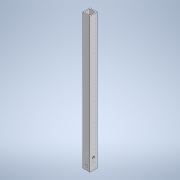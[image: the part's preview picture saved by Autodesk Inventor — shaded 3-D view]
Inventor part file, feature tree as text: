
AUTODESK INVENTOR PART (.ipt)
format: ipt  version: 2020.3 (Build 243373000, 373)  size: 143,360 bytes
history: native  units: mm
features: sketch x6, hole x5, other x1, extrude x1
ambient origin geometry x8: Origin, YZ Plane, XZ Plane, XY Plane, X Axis, Y Axis, Z Axis, Center Point
bodies: Body1 (feature_tree)
feature tree (13):
  other  "ソリッド1"
  extrude  "押し出し1"  Depth=9.0mm
  hole  "穴1"  [1 undecoded]
  hole  "穴2"  [1 undecoded]
  hole  "穴3"  [1 undecoded]
  hole  "穴4"  [1 undecoded]
  hole  "穴5"  [1 undecoded]
  sketch  "スケッチ1"
  sketch  "スケッチ2"
  sketch  "スケッチ3"
  sketch  "スケッチ4"
  sketch  "スケッチ5"
  sketch  "スケッチ6"
note: 5 required parameter values undecoded (feature->parameter linkage not recoverable at this tier; creation-order binding heuristic only, values carry confidence <= 0.55)
